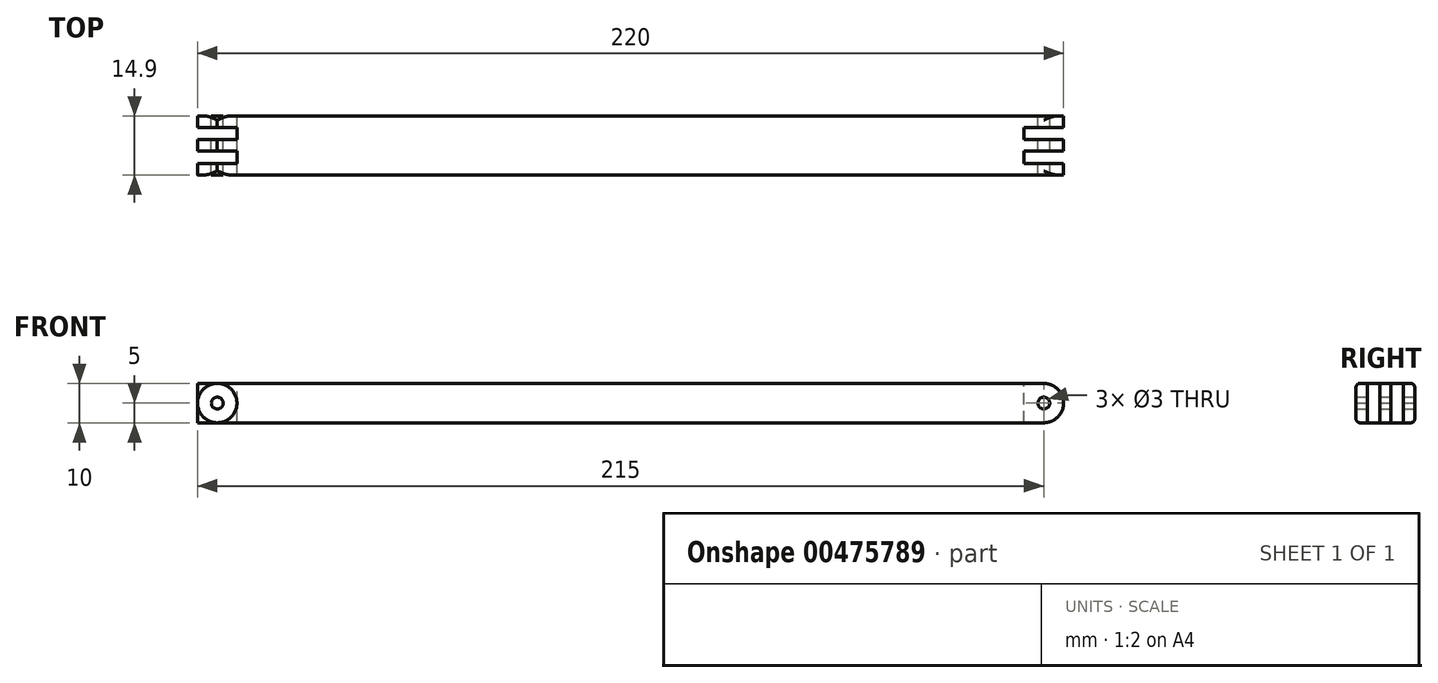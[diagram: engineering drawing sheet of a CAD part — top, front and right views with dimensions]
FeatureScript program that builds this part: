
annotation { "Feature Type Name" : "Feature", "Feature Type Description" : "" }
export const myFeature = defineFeature(function(context is Context, id is Id, definition is map)
    precondition{}
    {
        {
            var Q0;
            Q0=qCreatedBy(makeId("Front.planeOp"),FACE);
            var sketch = newSketch(context, id + "F0", { "sketchPlane" : qUnion([Q0])});
            skLineSegment(sketch, "E0.bottom", {"start": v(-100, 5) * mm, "end": v(100, 5) * mm});
            skLineSegment(sketch, "E0.top", {"start": v(-100, -5) * mm, "end": v(100, -5) * mm});
            skLineSegment(sketch, "E0.left", {"start": v(-100, 5) * mm, "end": v(-100, -5) * mm});
            skLineSegment(sketch, "E0.right", {"start": v(100, 5) * mm, "end": v(100, -5) * mm});
            skPoint(sketch, "E0.middle", {"position": v(0, 0) * mm});
            skSolve(sketch);
        }
        {
            var Q0;
            Q0=makeQuery(id+"F0.imprint","IMPRINT",FACE,{"disambiguationData":[TD([[makeQuery(id+"F0.imprint","IMPRINT",EDGE,{"derivedFrom":sQuery(id+"F0.wireOp",EDGE,"E0.bottom")}),-1.0]])]});
            extrude(context, id + "F1", {"entities" : qUnion([Q0]), "depth" : 14.9 * mm});
        }
        {
            var Q0;
            Q0=makeQuery(id+"F1.opExtrude","SWEPT_FACE",FACE,{"disambiguationData":[OSD([sQuery(id+"F0.wireOp",EDGE,"E0.bottom")])]});
            var sketch = newSketch(context, id + "F2", { "sketchPlane" : qUnion([Q0])});
            skLineSegment(sketch, "E1", {"start": v(-100, 0) * mm, "end": v(-110, 0) * mm});
            skLineSegment(sketch, "E2", {"start": v(-110, 0) * mm, "end": v(-110, -2.9) * mm});
            skLineSegment(sketch, "E3", {"start": v(-110, -2.9) * mm, "end": v(-100, -2.9) * mm});
            skLineSegment(sketch, "E4", {"start": v(-100, -6) * mm, "end": v(-110, -6) * mm});
            skLineSegment(sketch, "E5", {"start": v(-110, -6) * mm, "end": v(-110, -8.9) * mm});
            skLineSegment(sketch, "E6", {"start": v(-110, -8.9) * mm, "end": v(-100, -8.9) * mm});
            skLineSegment(sketch, "E7", {"start": v(-100, -14.9) * mm, "end": v(-110, -14.9) * mm});
            skLineSegment(sketch, "E8", {"start": v(-110, -14.9) * mm, "end": v(-110, -12) * mm});
            skLineSegment(sketch, "E9", {"start": v(-110, -12) * mm, "end": v(-100, -12) * mm});
            skLineSegment(sketch, "E10.MirrorCS", {"start": v(110, -6) * mm, "end": v(110, -8.9) * mm});
            skLineSegment(sketch, "E11.MirrorCS", {"start": v(110, -14.9) * mm, "end": v(110, -12) * mm});
            skLineSegment(sketch, "E12.MirrorCS", {"start": v(110, 0) * mm, "end": v(110, -2.9) * mm});
            skLineSegment(sketch, "E13.MirrorCS", {"start": v(100, -14.9) * mm, "end": v(110, -14.9) * mm});
            skLineSegment(sketch, "E14.MirrorCS", {"start": v(110, -12) * mm, "end": v(100, -12) * mm});
            skLineSegment(sketch, "E15.MirrorCS", {"start": v(100, -6) * mm, "end": v(110, -6) * mm});
            skLineSegment(sketch, "E16.MirrorCS", {"start": v(100, 0) * mm, "end": v(110, 0) * mm});
            skLineSegment(sketch, "E17.MirrorCS", {"start": v(110, -2.9) * mm, "end": v(100, -2.9) * mm});
            skLineSegment(sketch, "E18.MirrorCS", {"start": v(110, -8.9) * mm, "end": v(100, -8.9) * mm});
            skSolve(sketch);
        }
        {
            var Q0;
            {var subQ0=sQuery(id+"F2.wireOp",EDGE,"E7");Q0=makeQuery(id+"F2.imprint","IMPRINT",FACE,{"disambiguationData":[TD([[makeQuery(id+"F2.imprint","IMPRINT",EDGE,{"derivedFrom":subQ0}),-1.0]])]});}
            var Q1;
            {var subQ0=sQuery(id+"F2.wireOp",EDGE,"E4");Q1=makeQuery(id+"F2.imprint","IMPRINT",FACE,{"disambiguationData":[TD([[makeQuery(id+"F2.imprint","IMPRINT",EDGE,{"derivedFrom":subQ0}),1.0]])]});}
            var Q2;
            {var subQ0=sQuery(id+"F2.wireOp",EDGE,"E1");Q2=makeQuery(id+"F2.imprint","IMPRINT",FACE,{"disambiguationData":[TD([[makeQuery(id+"F2.imprint","IMPRINT",EDGE,{"derivedFrom":subQ0}),1.0]])]});}
            var Q3;
            Q3=makeQuery(id+"F2.imprint","IMPRINT",FACE,{"disambiguationData":[TD([[makeQuery(id+"F2.imprint","IMPRINT",EDGE,{"derivedFrom":sQuery(id+"F2.wireOp",EDGE,"E11.MirrorCS")}),1.0]])]});
            var Q4;
            Q4=makeQuery(id+"F2.imprint","IMPRINT",FACE,{"disambiguationData":[TD([[makeQuery(id+"F2.imprint","IMPRINT",EDGE,{"derivedFrom":sQuery(id+"F2.wireOp",EDGE,"E10.MirrorCS")}),-1.0]])]});
            var Q5;
            Q5=makeQuery(id+"F2.imprint","IMPRINT",FACE,{"disambiguationData":[TD([[makeQuery(id+"F2.imprint","IMPRINT",EDGE,{"derivedFrom":sQuery(id+"F2.wireOp",EDGE,"E12.MirrorCS")}),-1.0]])]});
            extrude(context, id + "F3", {"entities" : qUnion([Q0, Q1, Q2, Q3, Q4, Q5]), "operationType" : NewBodyOperationType.ADD, "oppositeDirection" : true, "depth" : 10 * mm});
        }
        {
            var Q0;
            Q0=makeQuery(id+"F3.boolean.opBoolean","MERGE",FACE,{"derivedFrom":[makeQuery(id+"F1.opExtrude","CAP_FACE",FACE,{"disambiguationData":[OSD([sQuery(id+"F0.wireOp",EDGE,"E0.bottom"),sQuery(id+"F0.wireOp",EDGE,"E0.top"),sQuery(id+"F0.wireOp",EDGE,"E0.left"),sQuery(id+"F0.wireOp",EDGE,"E0.right")])],"isStart":true}),makeQuery(id+"F3.opExtrude","SWEPT_FACE",FACE,{"disambiguationData":[OSD([sQuery(id+"F2.wireOp",EDGE,"E1")])]}),makeQuery(id+"F3.opExtrude","SWEPT_FACE",FACE,{"disambiguationData":[OSD([sQuery(id+"F2.wireOp",EDGE,"E16.MirrorCS")])]})]});
            var sketch = newSketch(context, id + "F4", { "sketchPlane" : qUnion([Q0])});
            skLineSegment(sketch, "E19", {"start": v(-110, 0) * mm, "end": v(110, 0) * mm, "construction": true});
            skCircle(sketch, "E20", {"center": v(-105, 0) * mm, "radius": 5 * mm});
            skCircle(sketch, "E21", {"center": v(-105, 0) * mm, "radius": 1.5 * mm});
            skLineSegment(sketch, "E22", {"start": v(-105, 5) * mm, "end": v(-105, 5) * mm});
            skLineSegment(sketch, "E23", {"start": v(-105, 5) * mm, "end": v(-105, -5) * mm, "construction": true});
            skLineSegment(sketch, "E24", {"start": v(-105, -5) * mm, "end": v(-105, -5) * mm});
            skLineSegment(sketch, "E25.MirrorCS", {"start": v(105, -5) * mm, "end": v(105, -5) * mm});
            skLineSegment(sketch, "E26.MirrorCS", {"start": v(105, 5) * mm, "end": v(105, 5) * mm});
            skLineSegment(sketch, "E27.MirrorCS", {"start": v(105, 5) * mm, "end": v(105, -5) * mm, "construction": true});
            skCircle(sketch, "E28.MirrorC", {"center": v(105, 0) * mm, "radius": 5 * mm});
            skCircle(sketch, "E29.MirrorC", {"center": v(105, 0) * mm, "radius": 1.5 * mm});
            skSolve(sketch);
        }
        {
            var Q0;
            {var subQ0=sQuery(id+"F4.wireOp",EDGE,"E20");var subQ1=sQuery(id+"F2.wireOp",EDGE,"E16.MirrorCS");var subQ2=makeQuery(id+"F3.opExtrude","SWEPT_EDGE",EDGE,{"disambiguationData":[OSD([sQuery(id+"F2.wireOp",EDGE,"E12.MirrorCS"),subQ1])]});var subQ3=makeQuery(id+"F4.imprint","INTERSECT",VERTEX,{"derivedFrom":[subQ2,subQ0]});Q0=makeQuery(id+"F4.imprint","IMPRINT",FACE,{"disambiguationData":[TD([[makeQuery(id+"F4.imprint","IMPRINT",EDGE,{"disambiguationData":[TD([[subQ3,1.0]])],"derivedFrom":subQ0}),-1.0]])]});}
            var Q1;
            {var subQ0=sQuery(id+"F4.wireOp",EDGE,"E20");var subQ1=sQuery(id+"F2.wireOp",EDGE,"E16.MirrorCS");var subQ2=makeQuery(id+"F3.opExtrude","SWEPT_EDGE",EDGE,{"disambiguationData":[OSD([sQuery(id+"F2.wireOp",EDGE,"E12.MirrorCS"),subQ1])]});var subQ3=makeQuery(id+"F4.imprint","INTERSECT",VERTEX,{"derivedFrom":[subQ2,subQ0]});Q1=makeQuery(id+"F4.imprint","IMPRINT",FACE,{"disambiguationData":[TD([[makeQuery(id+"F4.imprint","IMPRINT",EDGE,{"disambiguationData":[TD([[subQ3,-1.0]])],"derivedFrom":subQ0}),-1.0]])]});}
            var Q2;
            Q2=makeQuery(id+"F4.imprint","IMPRINT",FACE,{"disambiguationData":[TD([[makeQuery(id+"F4.imprint","IMPRINT",EDGE,{"derivedFrom":sQuery(id+"F4.wireOp",EDGE,"E21")}),1.0]])]});
            var Q3;
            {var subQ0=sQuery(id+"F4.wireOp",EDGE,"E28.MirrorC");var subQ1=sQuery(id+"F2.wireOp",EDGE,"E1");var subQ2=makeQuery(id+"F3.opExtrude","SWEPT_EDGE",EDGE,{"disambiguationData":[OSD([subQ1,sQuery(id+"F2.wireOp",EDGE,"E2")])]});var subQ3=makeQuery(id+"F4.imprint","INTERSECT",VERTEX,{"derivedFrom":[subQ2,subQ0]});Q3=makeQuery(id+"F4.imprint","IMPRINT",FACE,{"disambiguationData":[TD([[makeQuery(id+"F4.imprint","IMPRINT",EDGE,{"disambiguationData":[TD([[subQ3,-1.0]])],"derivedFrom":subQ0}),1.0]])]});}
            var Q4;
            {var subQ0=sQuery(id+"F4.wireOp",EDGE,"E28.MirrorC");var subQ1=sQuery(id+"F2.wireOp",EDGE,"E1");var subQ2=makeQuery(id+"F3.opExtrude","SWEPT_EDGE",EDGE,{"disambiguationData":[OSD([subQ1,sQuery(id+"F2.wireOp",EDGE,"E2")])]});var subQ3=makeQuery(id+"F4.imprint","INTERSECT",VERTEX,{"derivedFrom":[subQ2,subQ0]});Q4=makeQuery(id+"F4.imprint","IMPRINT",FACE,{"disambiguationData":[TD([[makeQuery(id+"F4.imprint","IMPRINT",EDGE,{"disambiguationData":[TD([[subQ3,1.0]])],"derivedFrom":subQ0}),1.0]])]});}
            var Q5;
            Q5=makeQuery(id+"F4.imprint","IMPRINT",FACE,{"disambiguationData":[TD([[makeQuery(id+"F4.imprint","IMPRINT",EDGE,{"derivedFrom":sQuery(id+"F4.wireOp",EDGE,"E29.MirrorC")}),-1.0]])]});
            extrude(context, id + "F5", {"entities" : qUnion([Q0, Q1, Q2, Q3, Q4, Q5]), "operationType" : NewBodyOperationType.REMOVE, "oppositeDirection" : true, "depth" : 14.9 * mm});
        }
        {
            var Q0;
            Q0=makeQuery(id+"F3.boolean.opBoolean","MERGE",EDGE,{"derivedFrom":[makeQuery(id+"F1.opExtrude","CAP_EDGE",EDGE,{"disambiguationData":[OSD([sQuery(id+"F0.wireOp",EDGE,"E0.top")])],"isStart":true}),makeQuery(id+"F3.opExtrude","CAP_EDGE",EDGE,{"disambiguationData":[OSD([sQuery(id+"F2.wireOp",EDGE,"E1")])],"isStart":false}),makeQuery(id+"F3.opExtrude","CAP_EDGE",EDGE,{"disambiguationData":[OSD([sQuery(id+"F2.wireOp",EDGE,"E16.MirrorCS")])],"isStart":false})]});
            var Q1;
            Q1=makeQuery(id+"F3.boolean.opBoolean","MERGE",EDGE,{"derivedFrom":[makeQuery(id+"F1.opExtrude","CAP_EDGE",EDGE,{"disambiguationData":[OSD([sQuery(id+"F0.wireOp",EDGE,"E0.bottom")])],"isStart":true}),makeQuery(id+"F3.opExtrude","CAP_EDGE",EDGE,{"disambiguationData":[OSD([sQuery(id+"F2.wireOp",EDGE,"E1")])],"isStart":true}),makeQuery(id+"F3.opExtrude","CAP_EDGE",EDGE,{"disambiguationData":[OSD([sQuery(id+"F2.wireOp",EDGE,"E16.MirrorCS")])],"isStart":true})]});
            var Q2;
            Q2=makeQuery(id+"F3.boolean.opBoolean","MERGE",EDGE,{"derivedFrom":[makeQuery(id+"F1.opExtrude","CAP_EDGE",EDGE,{"disambiguationData":[OSD([sQuery(id+"F0.wireOp",EDGE,"E0.top")])],"isStart":false}),makeQuery(id+"F3.opExtrude","CAP_EDGE",EDGE,{"disambiguationData":[OSD([sQuery(id+"F2.wireOp",EDGE,"E7")])],"isStart":false}),makeQuery(id+"F3.opExtrude","CAP_EDGE",EDGE,{"disambiguationData":[OSD([sQuery(id+"F2.wireOp",EDGE,"E13.MirrorCS")])],"isStart":false})]});
            var Q3;
            Q3=makeQuery(id+"F3.boolean.opBoolean","MERGE",EDGE,{"derivedFrom":[makeQuery(id+"F1.opExtrude","CAP_EDGE",EDGE,{"disambiguationData":[OSD([sQuery(id+"F0.wireOp",EDGE,"E0.bottom")])],"isStart":false}),makeQuery(id+"F3.opExtrude","CAP_EDGE",EDGE,{"disambiguationData":[OSD([sQuery(id+"F2.wireOp",EDGE,"E7")])],"isStart":true}),makeQuery(id+"F3.opExtrude","CAP_EDGE",EDGE,{"disambiguationData":[OSD([sQuery(id+"F2.wireOp",EDGE,"E13.MirrorCS")])],"isStart":true})]});
            fillet(context, id + "F6", {"entities" : qUnion([Q0, Q1, Q2, Q3]), "radius" : 1 * mm, "allowEdgeOverflow" : false});
        }
    });
